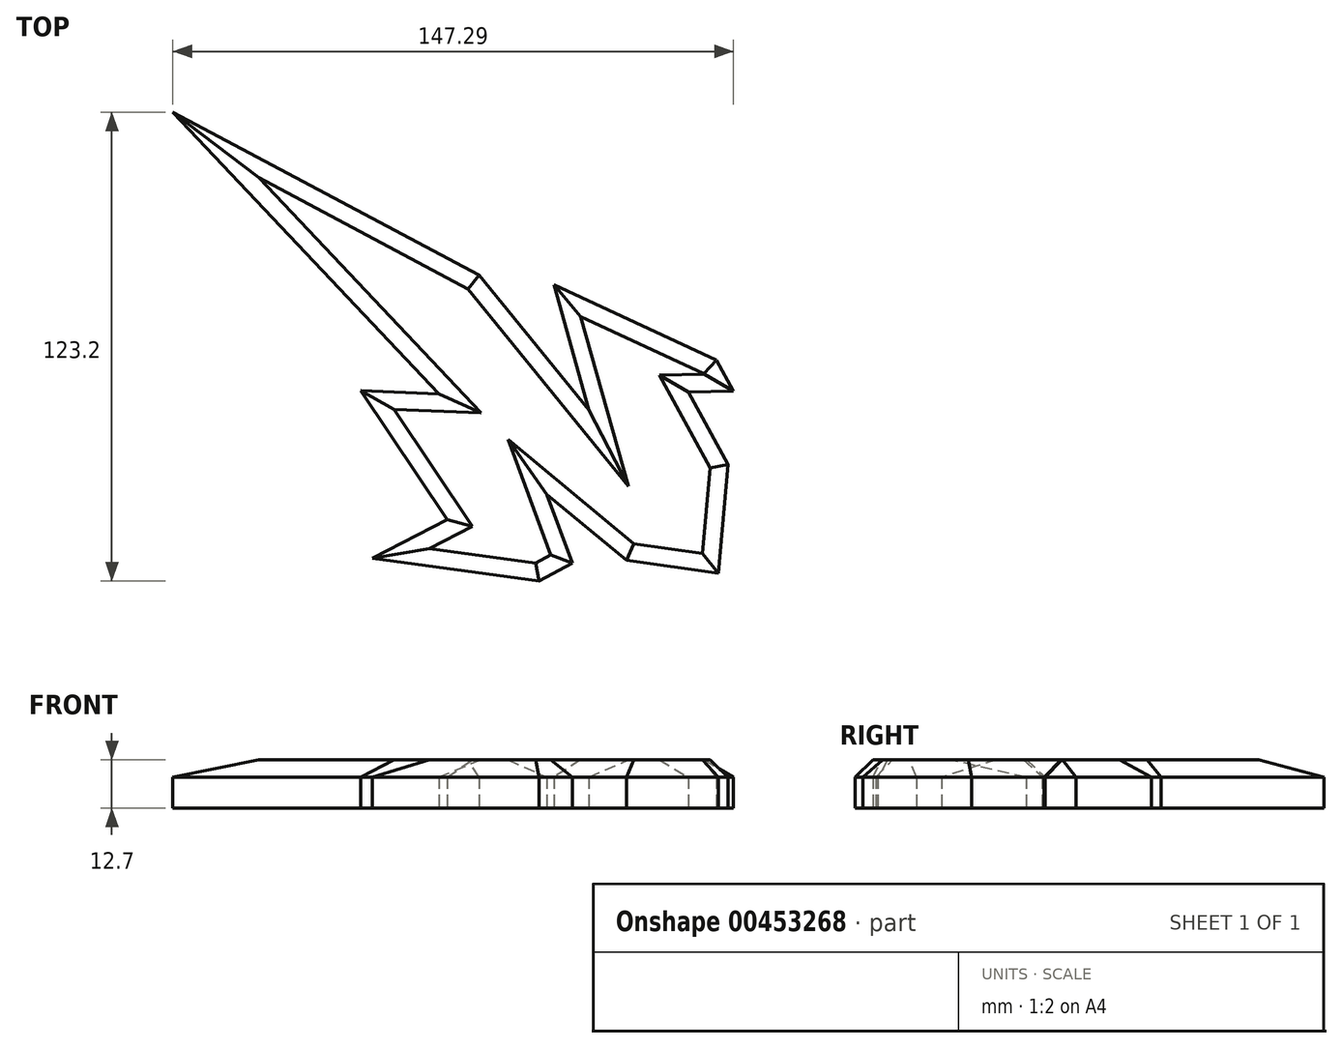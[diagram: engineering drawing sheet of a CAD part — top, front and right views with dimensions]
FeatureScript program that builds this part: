
annotation { "Feature Type Name" : "Feature", "Feature Type Description" : "" }
export const myFeature = defineFeature(function(context is Context, id is Id, definition is map)
    precondition{}
    {
        {
            var Q0;
            Q0=qCreatedBy(makeId("Top.planeOp"),FACE);
            var sketch = newSketch(context, id + "F0", { "sketchPlane" : qUnion([Q0])});
            skLineSegment(sketch, "E0", {"start": v(-54.12, 27.11) * mm, "end": v(-33.16, 9.79) * mm});
            skLineSegment(sketch, "E1", {"start": v(-5.1, 54.24) * mm, "end": v(-9.57, 62.36) * mm});
            skLineSegment(sketch, "E2", {"start": v(-9.57, 62.36) * mm, "end": v(-52.28, 82.15) * mm});
            skLineSegment(sketch, "E3", {"start": v(-152.38, 127.55) * mm, "end": v(-82.38, 53.54) * mm});
            skLineSegment(sketch, "E4", {"start": v(-152.38, 127.55) * mm, "end": v(-71.86, 84.68) * mm});
            skLineSegment(sketch, "E5", {"start": v(-71.86, 84.68) * mm, "end": v(-43.01, 49.24) * mm});
            skLineSegment(sketch, "E6", {"start": v(-5.1, 54.24) * mm, "end": v(-16.95, 54) * mm});
            skLineSegment(sketch, "E7", {"start": v(-102.98, 54.32) * mm, "end": v(-82.38, 53.54) * mm});
            skLineSegment(sketch, "E8", {"start": v(-102.98, 54.32) * mm, "end": v(-80.32, 20.43) * mm});
            skLineSegment(sketch, "E9", {"start": v(-80.32, 20.43) * mm, "end": v(-100, 10.3) * mm});
            skLineSegment(sketch, "E10", {"start": v(-100, 10.3) * mm, "end": v(-56.13, 4.35) * mm});
            skLineSegment(sketch, "E11", {"start": v(-54.12, 27.11) * mm, "end": v(-47.42, 9.08) * mm});
            skLineSegment(sketch, "E12", {"start": v(-47.42, 9.08) * mm, "end": v(-56.13, 4.35) * mm});
            skLineSegment(sketch, "E13", {"start": v(-33.16, 9.79) * mm, "end": v(-9.05, 6.43) * mm});
            skLineSegment(sketch, "E14", {"start": v(-6.52, 34.98) * mm, "end": v(-16.95, 54) * mm});
            skLineSegment(sketch, "E15", {"start": v(-9.05, 6.43) * mm, "end": v(-6.52, 34.98) * mm});
            skLineSegment(sketch, "E16", {"start": v(-43.01, 49.24) * mm, "end": v(-52.28, 82.15) * mm});
            skSolve(sketch);
        }
        {
            var Q0;
            Q0 = qSketchRegion(id + "FpxrbdjMyEjlgeR_4", true);
            var Q1;
            Q1 = qSketchRegion(id + "F0", true);
            var Q2;
            Q2 = qSketchRegion(id + "FTeMgZZDWwlIoI5_4", true);
            var Q3;
            Q3 = qSketchRegion(id + "FiezEiqxvGsPzSm_4", true);
            extrude(context, id + "F1", {"entities" : qUnion([Q0, Q1, Q2, Q3]), "depth" : 12.7 * mm});
        }
        {
            var Q0;
            Q0=makeQuery(id+"F1.opExtrude","CAP_FACE",FACE,{"disambiguationData":[OSD([sQuery(id+"F0.wireOp",EDGE,"ac24572f-c9b8-4898-8f51-4a96b5302339"),sQuery(id+"F0.wireOp",EDGE,"E0"),sQuery(id+"F0.wireOp",EDGE,"8ccd68a9-4c44-4eb3-822e-bd8bf68d1b1f"),sQuery(id+"F0.wireOp",EDGE,"8750759a-1506-4e7a-9516-fbbdf2d73f0c"),sQuery(id+"F0.wireOp",EDGE,"E1"),sQuery(id+"F0.wireOp",EDGE,"E2"),sQuery(id+"F0.wireOp",EDGE,"020dfb47-927a-47a1-aec1-821c8b549da0"),sQuery(id+"F0.wireOp",EDGE,"E3"),sQuery(id+"F0.wireOp",EDGE,"7c05c69a-53fe-4492-92a5-8393cd411d94"),sQuery(id+"F0.wireOp",EDGE,"E4"),sQuery(id+"F0.wireOp",EDGE,"E5"),sQuery(id+"F0.wireOp",EDGE,"E6"),sQuery(id+"F0.wireOp",EDGE,"c753dd7f-0135-4f19-810f-a6164e2e4ef6"),sQuery(id+"F0.wireOp",EDGE,"1b5e4ddd-4087-4e54-acc2-24082f5f2deb")])],"isStart":false});
            chamfer(context, id + "F2", {"entities" : qUnion([Q0]), "width" : 4.57 * mm, "tangentPropagation" : true});
        }
    });
